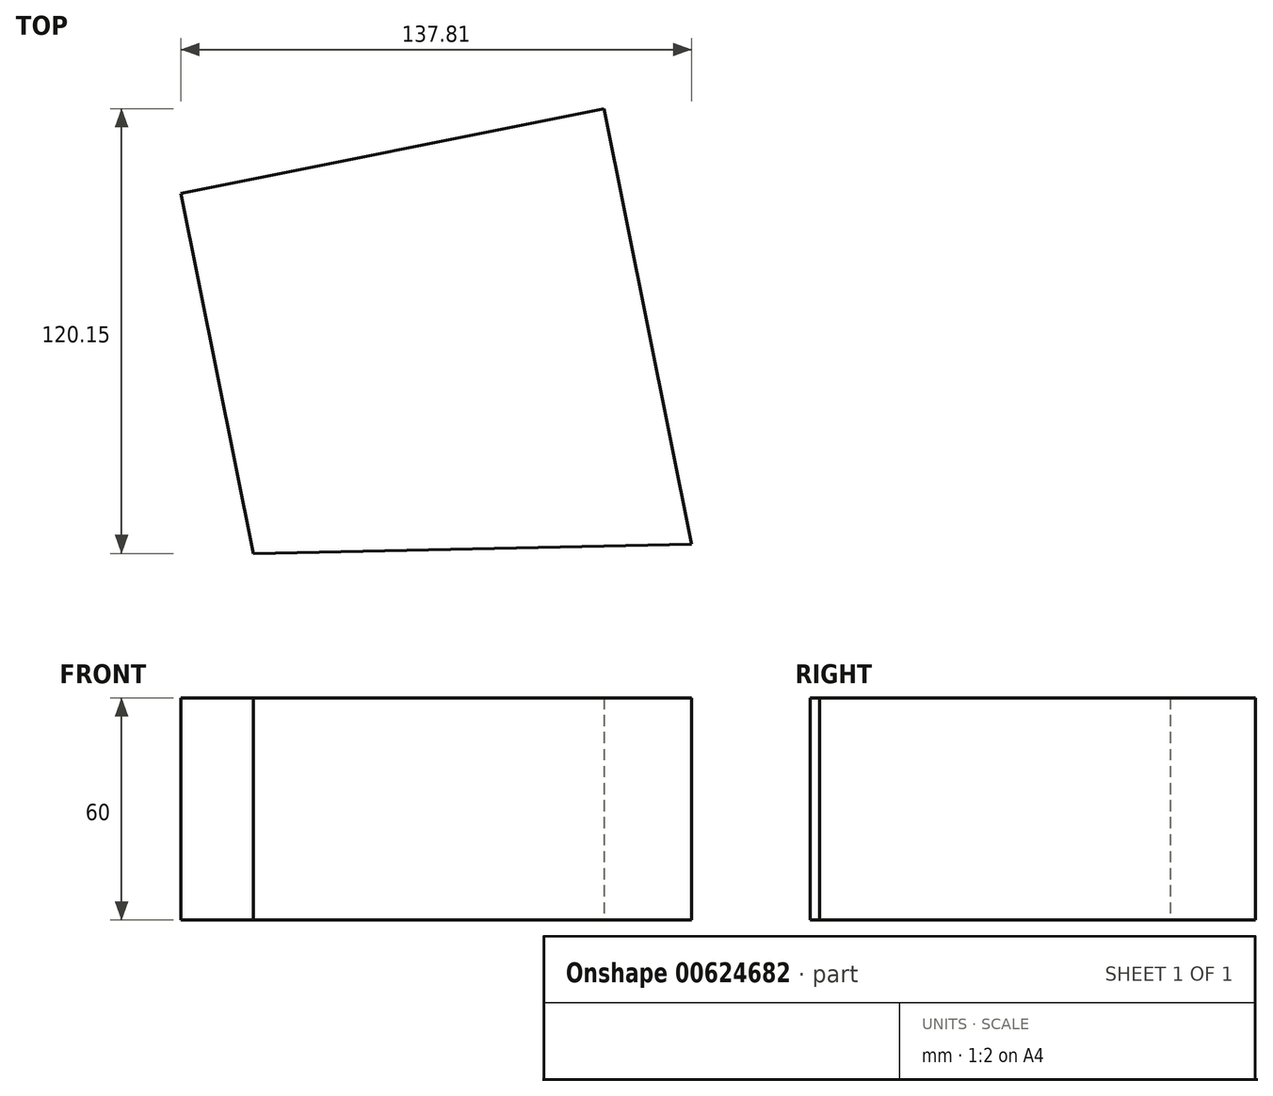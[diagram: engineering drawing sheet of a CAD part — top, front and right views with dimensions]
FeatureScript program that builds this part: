
annotation { "Feature Type Name" : "Feature", "Feature Type Description" : "" }
export const myFeature = defineFeature(function(context is Context, id is Id, definition is map)
    precondition{}
    {
        {
            var Q0;
            Q0=qCreatedBy(makeId("Top.planeOp"),FACE);
            var sketch = newSketch(context, id + "F0", { "sketchPlane" : qUnion([Q0])});
            skLineSegment(sketch, "E0", {"start": v(-46.2, -48) * mm, "end": v(-65.74, 49.2) * mm});
            skLineSegment(sketch, "E1", {"start": v(-65.74, 49.2) * mm, "end": v(48.42, 72.15) * mm});
            skLineSegment(sketch, "E2", {"start": v(48.42, 72.15) * mm, "end": v(72.07, -45.5) * mm});
            skLineSegment(sketch, "E3", {"start": v(72.07, -45.5) * mm, "end": v(-46.2, -48) * mm});
            skSolve(sketch);
        }
        {
            var Q0;
            Q0=makeQuery(id+"F0.imprint","IMPRINT",FACE,{"disambiguationData":[TD([[makeQuery(id+"F0.imprint","IMPRINT",EDGE,{"derivedFrom":sQuery(id+"F0.wireOp",EDGE,"E0")}),-1.0]])]});
            extrude(context, id + "F1", {"entities" : qUnion([Q0]), "depth" : 60 * mm, "offsetDistance" : 25 * mm});
        }
    });
